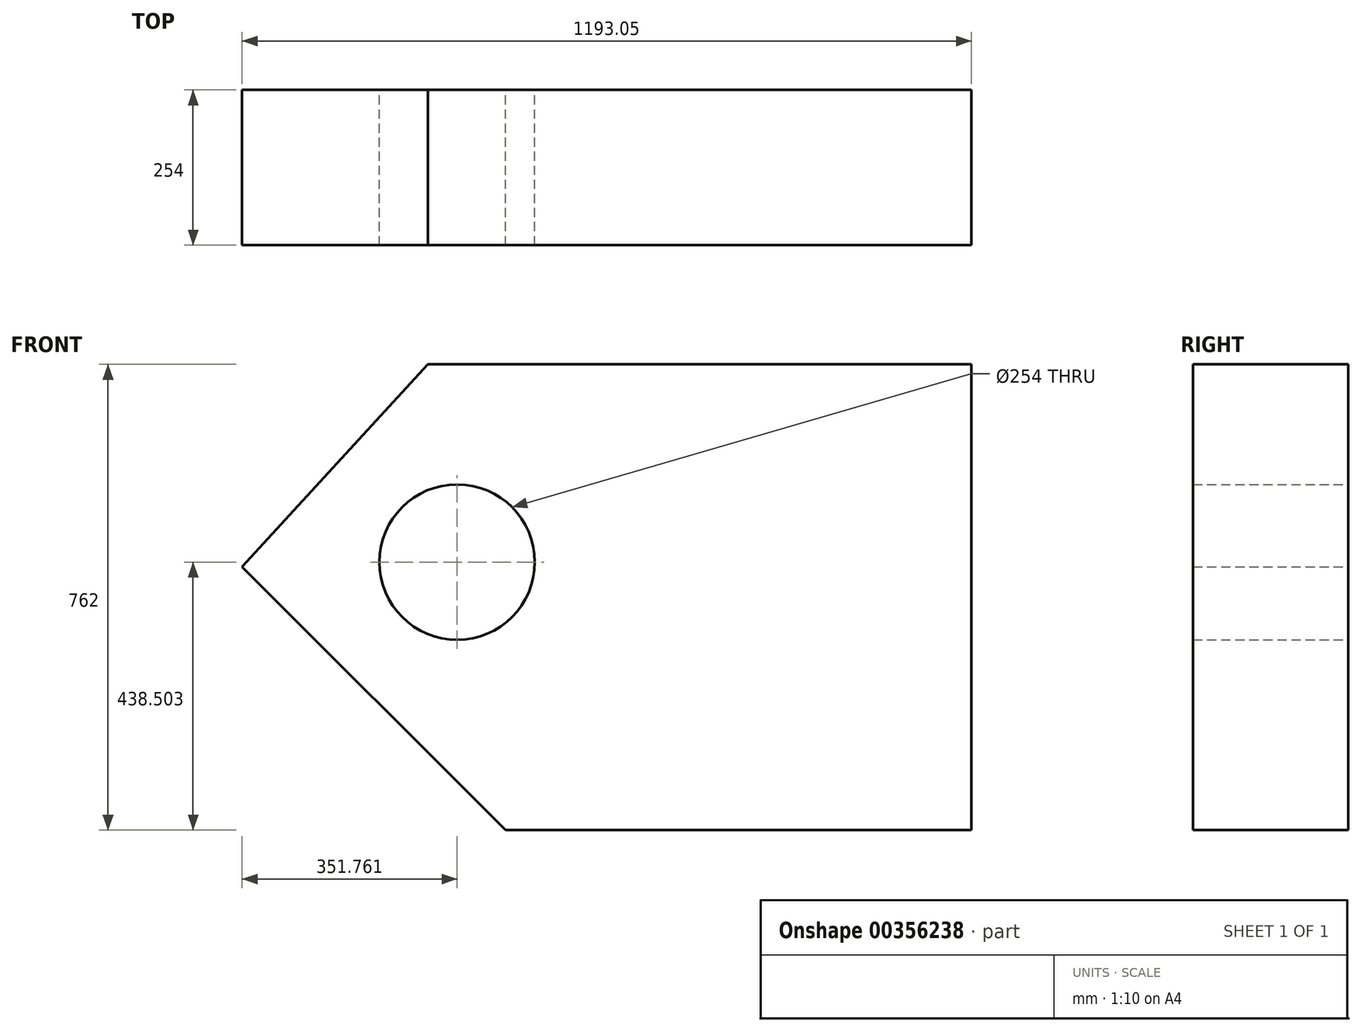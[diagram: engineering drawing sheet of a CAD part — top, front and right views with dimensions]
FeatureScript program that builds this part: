
annotation { "Feature Type Name" : "Feature", "Feature Type Description" : "" }
export const myFeature = defineFeature(function(context is Context, id is Id, definition is map)
    precondition{}
    {
        {
            var Q0;
            Q0=qCreatedBy(makeId("Front.planeOp"),FACE);
            var sketch = newSketch(context, id + "F0", { "sketchPlane" : qUnion([Q0])});
            skLineSegment(sketch, "E0", {"start": v(-421.87, -48.66) * mm, "end": v(467.13, -48.66) * mm});
            skLineSegment(sketch, "E1", {"start": v(467.13, -48.66) * mm, "end": v(467.13, -810.66) * mm});
            skLineSegment(sketch, "E2", {"start": v(467.13, -810.66) * mm, "end": v(-294.87, -810.66) * mm});
            skLineSegment(sketch, "E3", {"start": v(-294.87, -810.66) * mm, "end": v(-725.92, -379.6) * mm});
            skLineSegment(sketch, "E4", {"start": v(-421.87, -48.66) * mm, "end": v(-725.92, -379.6) * mm});
            skCircle(sketch, "E5", {"center": v(-374.16, -372.16) * mm, "radius": 127 * mm});
            skSolve(sketch);
        }
        {
            var Q0;
            Q0=makeQuery(id+"F0.imprint","IMPRINT",FACE,{"disambiguationData":[TD([[makeQuery(id+"F0.imprint","IMPRINT",EDGE,{"derivedFrom":sQuery(id+"F0.wireOp",EDGE,"E0")}),-1.0]])]});
            extrude(context, id + "F1", {"entities" : qUnion([Q0]), "depth" : 254 * mm});
        }
    });
